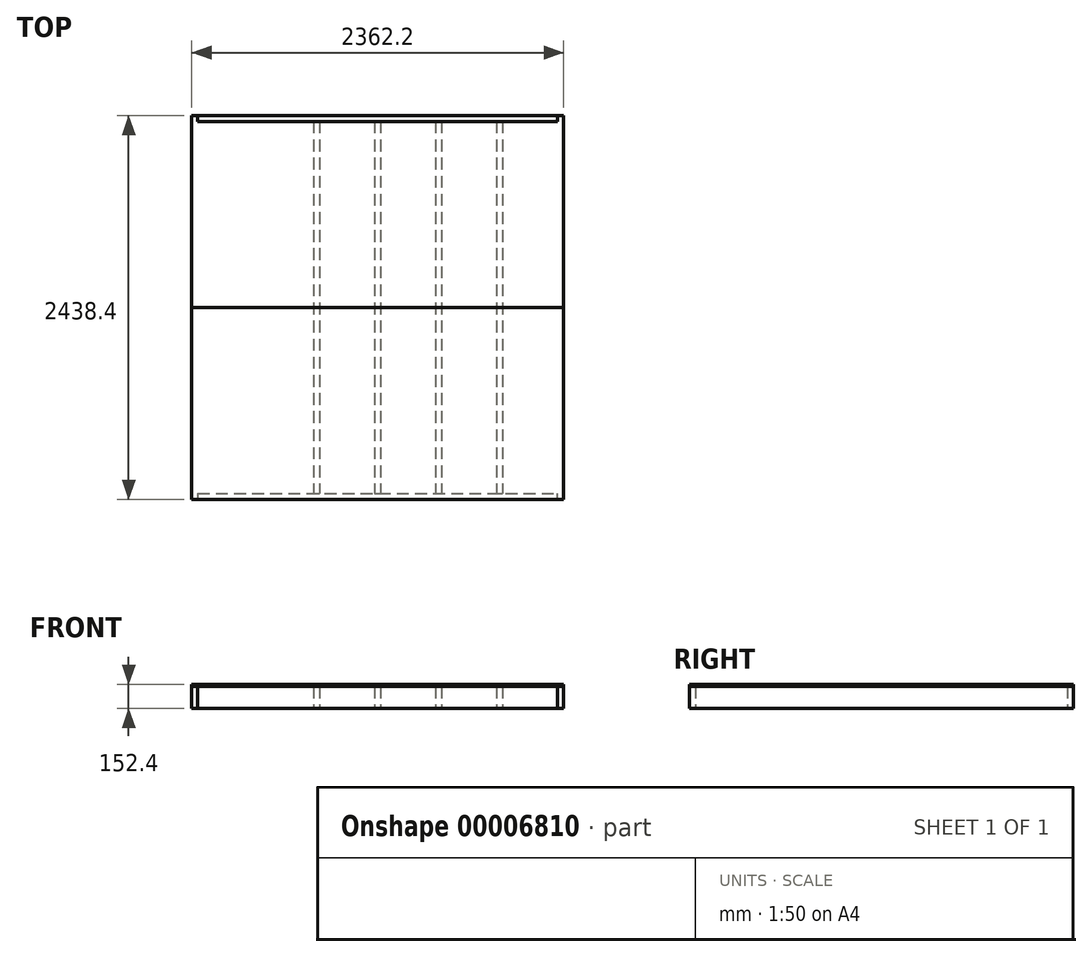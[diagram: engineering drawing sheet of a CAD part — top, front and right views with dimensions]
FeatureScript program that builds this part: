
annotation { "Feature Type Name" : "Feature", "Feature Type Description" : "" }
export const myFeature = defineFeature(function(context is Context, id is Id, definition is map)
    precondition{}
    {
        {
            var Q0;
            Q0=qCreatedBy(makeId("Top.planeOp"),FACE);
            var sketch = newSketch(context, id + "F0", { "sketchPlane" : qUnion([Q0])});
            skLineSegment(sketch, "E0.rect.bottom", {"start": v(1181.1, 1219.2) * mm, "end": v(-1181.1, 1219.2) * mm, "construction": true});
            skLineSegment(sketch, "E0.rect.top", {"start": v(1181.1, -1219.2) * mm, "end": v(-1181.1, -1219.2) * mm, "construction": true});
            skLineSegment(sketch, "E0.rect.left", {"start": v(1181.1, 1219.2) * mm, "end": v(1181.1, -1219.2) * mm, "construction": true});
            skLineSegment(sketch, "E0.rect.right", {"start": v(-1181.1, 1219.2) * mm, "end": v(-1181.1, -1219.2) * mm, "construction": true});
            skPoint(sketch, "E0.rect.middle", {"position": v(0, 0) * mm});
            skLineSegment(sketch, "E1.bottom", {"start": v(-1181.1, 1219.2) * mm, "end": v(-1143, 1219.2) * mm});
            skLineSegment(sketch, "E1.top", {"start": v(-1181.1, -1219.2) * mm, "end": v(-1143, -1219.2) * mm});
            skLineSegment(sketch, "E1.left", {"start": v(-1181.1, 1219.2) * mm, "end": v(-1181.1, -1219.2) * mm});
            skLineSegment(sketch, "E1.right", {"start": v(-1143, 1219.2) * mm, "end": v(-1143, -1219.2) * mm});
            skLineSegment(sketch, "E2.bottom", {"start": v(1181.1, -1219.2) * mm, "end": v(1143, -1219.2) * mm});
            skLineSegment(sketch, "E2.top", {"start": v(1181.1, 1219.2) * mm, "end": v(1143, 1219.2) * mm});
            skLineSegment(sketch, "E2.left", {"start": v(1181.1, -1219.2) * mm, "end": v(1181.1, 1219.2) * mm});
            skLineSegment(sketch, "E2.right", {"start": v(1143, -1219.2) * mm, "end": v(1143, 1219.2) * mm});
            skLineSegment(sketch, "E3.bottom", {"start": v(-1143, 1219.2) * mm, "end": v(1143, 1219.2) * mm});
            skLineSegment(sketch, "E3.top", {"start": v(-1143, 1181.1) * mm, "end": v(1143, 1181.1) * mm});
            skLineSegment(sketch, "E3.left", {"start": v(-1143, 1219.2) * mm, "end": v(-1143, 1181.1) * mm});
            skLineSegment(sketch, "E3.right", {"start": v(1143, 1219.2) * mm, "end": v(1143, 1181.1) * mm});
            skLineSegment(sketch, "E4.bottom", {"start": v(-1143, -1219.2) * mm, "end": v(1143, -1219.2) * mm});
            skLineSegment(sketch, "E4.top", {"start": v(-1143, -1181.1) * mm, "end": v(1143, -1181.1) * mm});
            skLineSegment(sketch, "E4.left", {"start": v(-1143, -1219.2) * mm, "end": v(-1143, -1181.1) * mm});
            skLineSegment(sketch, "E4.right", {"start": v(1143, -1219.2) * mm, "end": v(1143, -1181.1) * mm});
            skLineSegment(sketch, "E5.bottom", {"start": v(-793.75, 1181.1) * mm, "end": v(-755.65, 1181.1) * mm});
            skLineSegment(sketch, "E5.top", {"start": v(-793.75, -1181.1) * mm, "end": v(-755.65, -1181.1) * mm});
            skLineSegment(sketch, "E5.left", {"start": v(-793.75, 1181.1) * mm, "end": v(-793.75, -1181.1) * mm});
            skLineSegment(sketch, "E5.right", {"start": v(-755.65, 1181.1) * mm, "end": v(-755.65, -1181.1) * mm});
            skLineSegment(sketch, "E6.1.0.0", {"start": v(-406.4, 1181.1) * mm, "end": v(-406.4, -1181.1) * mm});
            skLineSegment(sketch, "E6.1.0.1", {"start": v(-368.3, 1181.1) * mm, "end": v(-368.3, -1181.1) * mm});
            skLineSegment(sketch, "E6.2.0.0", {"start": v(-19.05, 1181.1) * mm, "end": v(-19.05, -1181.1) * mm});
            skLineSegment(sketch, "E6.2.0.1", {"start": v(19.05, 1181.1) * mm, "end": v(19.05, -1181.1) * mm});
            skLineSegment(sketch, "E6.3.0.0", {"start": v(368.3, 1181.1) * mm, "end": v(368.3, -1181.1) * mm});
            skLineSegment(sketch, "E6.3.0.1", {"start": v(406.4, 1181.1) * mm, "end": v(406.4, -1181.1) * mm});
            skLineSegment(sketch, "E6.direction1", {"start": v(-793.75, -1181.1) * mm, "end": v(-406.4, -1181.1) * mm, "construction": true});
            skLineSegment(sketch, "E7.0.4.0", {"start": v(755.65, 1181.1) * mm, "end": v(755.65, -1181.1) * mm});
            skLineSegment(sketch, "E7.3.4.0", {"start": v(793.75, 1181.1) * mm, "end": v(793.75, -1181.1) * mm});
            skSolve(sketch);
        }
        {
            var Q0;
            Q0=makeQuery(id+"F0.imprint","IMPRINT",FACE,{"disambiguationData":[TD([[makeQuery(id+"F0.imprint","IMPRINT",EDGE,{"derivedFrom":sQuery(id+"F0.wireOp",EDGE,"E1.bottom")}),-1.0]])]});
            var Q1;
            Q1=makeQuery(id+"F0.imprint","IMPRINT",FACE,{"disambiguationData":[TD([[makeQuery(id+"F0.imprint","IMPRINT",EDGE,{"derivedFrom":sQuery(id+"F0.wireOp",EDGE,"E5.bottom")}),-1.0]])]});
            var Q2;
            {var subQ2=sQuery(id+"F0.wireOp",EDGE,"E6.1.0.0");Q2=makeQuery(id+"F0.imprint","IMPRINT",FACE,{"disambiguationData":[TD([[makeQuery(id+"F0.imprint","IMPRINT",EDGE,{"derivedFrom":subQ2}),1.0]])]});}
            var Q3;
            {var subQ1=sQuery(id+"F0.wireOp",EDGE,"E6.2.0.0");Q3=makeQuery(id+"F0.imprint","IMPRINT",FACE,{"disambiguationData":[TD([[makeQuery(id+"F0.imprint","IMPRINT",EDGE,{"derivedFrom":subQ1}),1.0]])]});}
            var Q4;
            {var subQ1=sQuery(id+"F0.wireOp",EDGE,"E6.3.0.0");Q4=makeQuery(id+"F0.imprint","IMPRINT",FACE,{"disambiguationData":[TD([[makeQuery(id+"F0.imprint","IMPRINT",EDGE,{"derivedFrom":subQ1}),1.0]])]});}
            var Q5;
            Q5=makeQuery(id+"F0.imprint","IMPRINT",FACE,{"disambiguationData":[TD([[makeQuery(id+"F0.imprint","IMPRINT",EDGE,{"derivedFrom":sQuery(id+"F0.wireOp",EDGE,"E2.bottom")}),-1.0]])]});
            var Q6;
            {var subQ1=sQuery(id+"F0.wireOp",EDGE,"E7.0.4.0");Q6=makeQuery(id+"F0.imprint","IMPRINT",FACE,{"disambiguationData":[TD([[makeQuery(id+"F0.imprint","IMPRINT",EDGE,{"derivedFrom":subQ1}),1.0]])]});}
            extrude(context, id + "F1", {"entities" : qUnion([Q0, Q1, Q2, Q3, Q4, Q5, Q6]), "depth" : 139.7 * mm});
        }
        {
            var Q0;
            Q0=makeQuery(id+"F0.imprint","IMPRINT",FACE,{"disambiguationData":[TD([[makeQuery(id+"F0.imprint","IMPRINT",EDGE,{"derivedFrom":sQuery(id+"F0.wireOp",EDGE,"E3.bottom")}),-1.0]])]});
            var Q1;
            Q1=makeQuery(id+"F0.imprint","IMPRINT",FACE,{"disambiguationData":[TD([[makeQuery(id+"F0.imprint","IMPRINT",EDGE,{"derivedFrom":sQuery(id+"F0.wireOp",EDGE,"E4.bottom")}),1.0]])]});
            extrude(context, id + "F2", {"entities" : qUnion([Q0, Q1]), "depth" : 139.7 * mm});
        }
        {
            var Q0;
            Q0=makeQuery(id+"F2.opExtrude","CAP_FACE",FACE,{"disambiguationData":[OSD([sQuery(id+"F0.wireOp",EDGE,"E3.bottom"),sQuery(id+"F0.wireOp",EDGE,"E3.top"),sQuery(id+"F0.wireOp",EDGE,"E3.left"),sQuery(id+"F0.wireOp",EDGE,"E3.right"),sQuery(id+"F0.wireOp",EDGE,"E5.bottom")])],"isStart":false});
            var sketch = newSketch(context, id + "F3", { "sketchPlane" : qUnion([Q0])});
            skPoint(sketch, "E8.0", {"position": v(1181.1, 1219.2) * mm});
            skLineSegment(sketch, "E9.left", {"start": v(1181.1, 1219.2) * mm, "end": v(1181.1, -1219.2) * mm});
            skPoint(sketch, "E10.0", {"position": v(-1181.1, -1219.2) * mm});
            skLineSegment(sketch, "E11.right", {"start": v(-1181.1, 1219.2) * mm, "end": v(-1181.1, -1219.2) * mm});
            skLineSegment(sketch, "E12", {"start": v(-1181.1, 0) * mm, "end": v(1181.1, 0) * mm});
            skLineSegment(sketch, "E13", {"start": v(-1181.1, 1219.2) * mm, "end": v(1181.1, 1219.2) * mm});
            skLineSegment(sketch, "E14", {"start": v(-1181.1, -1219.2) * mm, "end": v(1181.1, -1219.2) * mm});
            skSolve(sketch);
        }
        {
            var Q0;
            {var subQ4=sQuery(id+"F3.wireOp",EDGE,"E9.top");Q0=makeQuery(id+"F3.imprint","IMPRINT",FACE,{"disambiguationData":[TD([[makeQuery(id+"F3.imprint","IMPRINT",EDGE,{"derivedFrom":subQ4}),-1.0]])]});}
            var Q1;
            {var subQ0=sQuery(id+"F3.wireOp",EDGE,"E12");Q1=makeQuery(id+"F3.imprint","IMPRINT",FACE,{"disambiguationData":[TD([[makeQuery(id+"F3.imprint","IMPRINT",EDGE,{"derivedFrom":subQ0}),-1.0]])]});}
            extrude(context, id + "F4", {"entities" : qUnion([Q0, Q1]), "depth" : 12.7 * mm});
        }
        {
            var Q0;
            {var subQ5=sQuery(id+"F3.wireOp",EDGE,"E11.top");Q0=makeQuery(id+"F3.imprint","IMPRINT",FACE,{"disambiguationData":[TD([[makeQuery(id+"F3.imprint","IMPRINT",EDGE,{"derivedFrom":subQ5}),-1.0]])]});}
            var Q1;
            {var subQ0=makeQuery(id+"F2.opExtrude","CAP_EDGE",EDGE,{"disambiguationData":[OSD([sQuery(id+"F0.wireOp",EDGE,"E3.left")])],"isStart":false});Q1=makeQuery(id+"F3.imprint","IMPRINT",FACE,{"disambiguationData":[TD([[makeQuery(id+"F3.imprint","IMPRINT",EDGE,{"derivedFrom":subQ0}),1.0]])]});}
            var Q2;
            {var subQ7=sQuery(id+"F3.wireOp",EDGE,"E12");Q2=makeQuery(id+"F3.imprint","IMPRINT",FACE,{"disambiguationData":[TD([[makeQuery(id+"F3.imprint","IMPRINT",EDGE,{"derivedFrom":subQ7}),1.0]])]});}
            extrude(context, id + "F5", {"entities" : qUnion([Q0, Q1, Q2]), "depth" : 12.7 * mm});
        }
    });
